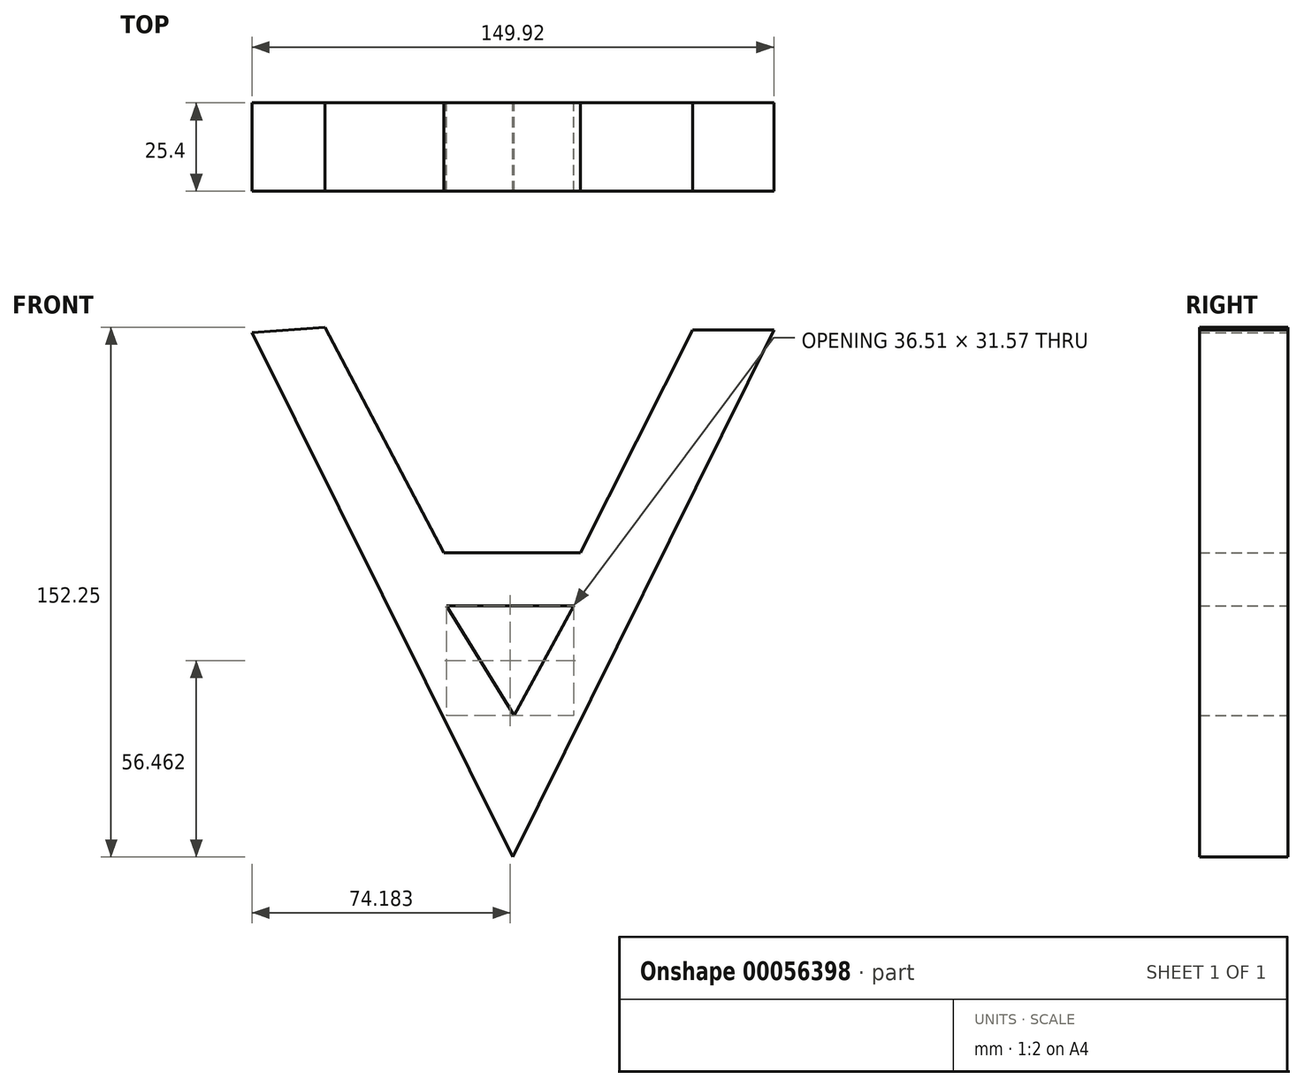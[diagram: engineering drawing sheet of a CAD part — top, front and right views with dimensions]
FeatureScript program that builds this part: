
annotation { "Feature Type Name" : "Feature", "Feature Type Description" : "" }
export const myFeature = defineFeature(function(context is Context, id is Id, definition is map)
    precondition{}
    {
        {
            var Q0;
            Q0=qCreatedBy(makeId("Front.planeOp"),FACE);
            var sketch = newSketch(context, id + "F0", { "sketchPlane" : qUnion([Q0])});
            skLineSegment(sketch, "E0", {"start": v(-74.96, 74.96) * mm, "end": v(0, -75.74) * mm});
            skLineSegment(sketch, "E1", {"start": v(0, -75.74) * mm, "end": v(74.96, 75.74) * mm});
            skLineSegment(sketch, "E2", {"start": v(74.96, 75.74) * mm, "end": v(51.66, 75.74) * mm});
            skLineSegment(sketch, "E3", {"start": v(51.66, 75.74) * mm, "end": v(19.42, 11.65) * mm});
            skLineSegment(sketch, "E4", {"start": v(19.42, 11.65) * mm, "end": v(-19.8, 11.65) * mm});
            skLineSegment(sketch, "E5", {"start": v(-19.8, 11.65) * mm, "end": v(-53.99, 76.51) * mm});
            skLineSegment(sketch, "E6", {"start": v(-53.99, 76.51) * mm, "end": v(-74.96, 74.96) * mm});
            skLineSegment(sketch, "E7", {"start": v(-19.03, -3.5) * mm, "end": v(17.48, -3.5) * mm});
            skLineSegment(sketch, "E8", {"start": v(17.48, -3.5) * mm, "end": v(0, -35.73) * mm});
            skLineSegment(sketch, "E9", {"start": v(0.78, -35.73) * mm, "end": v(-19.03, -3.5) * mm});
            skSolve(sketch);
        }
        {
            var Q0;
            Q0 = qSketchRegion(id + "F0", true);
            extrude(context, id + "F1", {"entities" : qUnion([Q0]), "depth" : 25.4 * mm});
        }
    });
